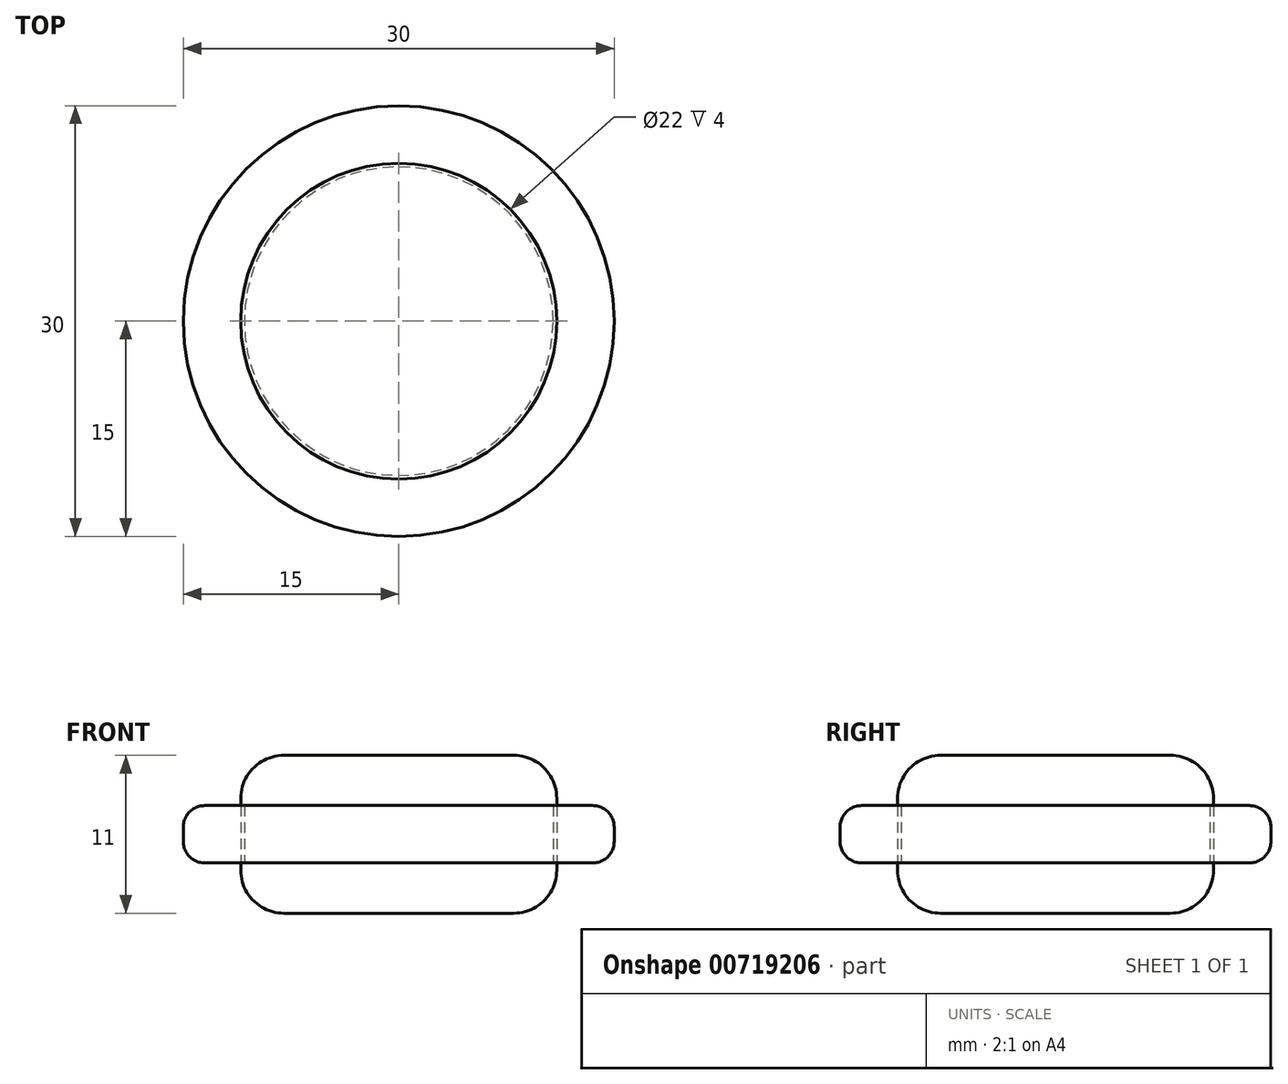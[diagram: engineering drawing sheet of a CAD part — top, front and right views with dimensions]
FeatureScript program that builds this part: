
annotation { "Feature Type Name" : "Feature", "Feature Type Description" : "" }
export const myFeature = defineFeature(function(context is Context, id is Id, definition is map)
    precondition{}
    {
        {
            assignVariable(context, id + "F0", {"name" : "depth", "anyValue" : 4 * mm});
        }
        {
            assignVariable(context, id + "F1", {"name" : "height", "anyValue" : 11 * mm});
        }
        {
            var Q0;
            Q0=qCreatedBy(makeId("Top.planeOp"),FACE);
            var sketch = newSketch(context, id + "F2", { "sketchPlane" : qUnion([Q0])});
            skCircle(sketch, "E0", {"center": v(0, 0) * mm, "radius": 15 * mm});
            skCircle(sketch, "E1", {"center": v(0, 0) * mm, "radius": 11 * mm});
            skSolve(sketch);
        }
        {
            var Q0;
            Q0=makeQuery(id+"F2.imprint","IMPRINT",FACE,{"disambiguationData":[TD([[makeQuery(id+"F2.imprint","IMPRINT",EDGE,{"derivedFrom":sQuery(id+"F2.wireOp",EDGE,"E0")}),1.0]])]});
            extrude(context, id + "F3", {"entities" : qUnion([Q0]), "endBound" : BoundingType.SYMMETRIC, "depth" : getVariable(context, 'depth'), "offsetDistance" : 25 * mm});
        }
        {
            var Q0;
            Q0=qCreatedBy(makeId("Top.planeOp"),FACE);
            var sketch = newSketch(context, id + "F4", { "sketchPlane" : qUnion([Q0])});
            skCircle(sketch, "E2", {"center": v(0, 0) * mm, "radius": 11 * mm});
            skSolve(sketch);
        }
        {
            var Q0;
            Q0=qSketchRegion(id+"F4",true);
            extrude(context, id + "F5", {"entities" : qUnion([Q0]), "endBound" : BoundingType.SYMMETRIC, "depth" : getVariable(context, 'height'), "offsetDistance" : 25 * mm});
        }
        {
            var Q0;
            Q0=makeQuery(id+"F5.opExtrude","CAP_FACE",FACE,{"disambiguationData":[OSD([sQuery(id+"F4.wireOp",EDGE,"E2")])],"isStart":false});
            var Q1;
            Q1=makeQuery(id+"F5.opExtrude","CAP_FACE",FACE,{"disambiguationData":[OSD([sQuery(id+"F4.wireOp",EDGE,"E2")])],"isStart":true});
            fillet(context, id + "F6", {"entities" : qUnion([Q0, Q1]), "radius" : 3 * mm, "tangentPropagation" : true, "allowEdgeOverflow" : false});
        }
        {
            var Q0;
            Q0=makeQuery(id+"F3.opExtrude","SWEPT_FACE",FACE,{"disambiguationData":[OSD([sQuery(id+"F2.wireOp",EDGE,"E0")])]});
            fillet(context, id + "F7", {"entities" : qUnion([Q0]), "radius" : 1.5 * mm, "tangentPropagation" : true, "allowEdgeOverflow" : false});
        }
        {
            var Q0;
            Q0=qCreatedBy(makeId("Top.planeOp"),FACE);
            var sketch = newSketch(context, id + "F8", { "sketchPlane" : qUnion([Q0])});
            skCircle(sketch, "E3", {"center": v(0, 0) * mm, "radius": 15 * mm});
            skCircle(sketch, "E4", {"center": v(0, 0) * mm, "radius": 10.75 * mm});
            skSolve(sketch);
        }
        {
            var Q0;
            Q0 = qSketchRegion(id + "F8", true);
            extrude(context, id + "F9", {"entities" : qUnion([Q0]), "endBound" : BoundingType.SYMMETRIC, "depth" : getVariable(context, 'depth'), "offsetDistance" : 25 * mm});
        }
        {
            var Q0;
            Q0=makeQuery(id+"F9.opExtrude","SWEPT_BODY",BODY,{"disambiguationData":[OSD([sQuery(id+"F8.wireOp",EDGE,"E3"),sQuery(id+"F8.wireOp",EDGE,"E4")])]});
            var Q1;
            Q1=makeQuery(id+"F5.opExtrude","SWEPT_BODY",BODY,{"disambiguationData":[OSD([sQuery(id+"F4.wireOp",EDGE,"E2")])]});
            booleanBodies(context, id + "F10", {"operationType" : BooleanOperationType.SUBTRACTION, "tools" : qUnion([Q0]), "targets" : qUnion([Q1])});
        }
    });
